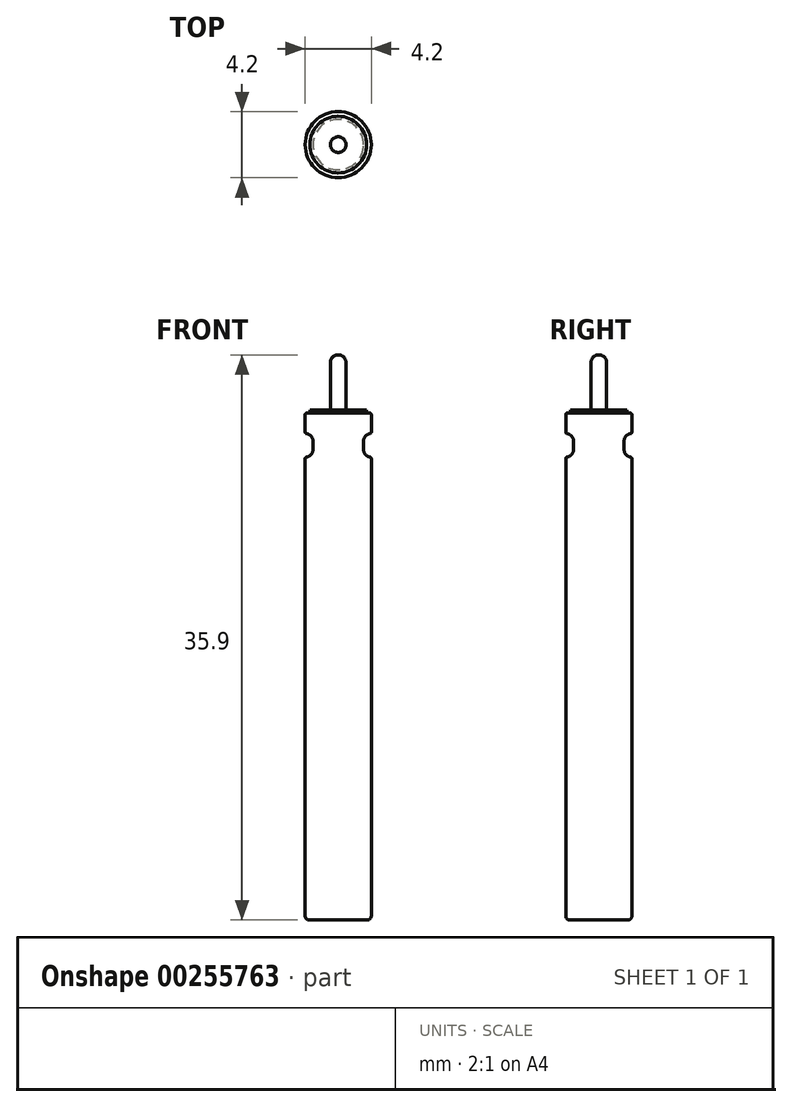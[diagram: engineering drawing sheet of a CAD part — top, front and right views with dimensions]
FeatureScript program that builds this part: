
annotation { "Feature Type Name" : "Feature", "Feature Type Description" : "" }
export const myFeature = defineFeature(function(context is Context, id is Id, definition is map)
    precondition{}
    {
        {
            var Q0;
            Q0=qCreatedBy(makeId("Front.planeOp"),FACE);
            var sketch = newSketch(context, id + "F0", { "sketchPlane" : qUnion([Q0])});
            skLineSegment(sketch, "E0", {"start": v(0, 3.7) * mm, "end": v(0, -32.2) * mm});
            skLineSegment(sketch, "E1", {"start": v(0, -32.2) * mm, "end": v(1.85, -32.2) * mm});
            skLineSegment(sketch, "E2", {"start": v(2.1, -31.95) * mm, "end": v(2.1, -2.8) * mm});
            skLineSegment(sketch, "E3", {"start": v(2.1, -2.8) * mm, "end": v(2.1, -2.8) * mm});
            skLineSegment(sketch, "E4", {"start": v(1.6, -2.3) * mm, "end": v(1.6, -1.8) * mm});
            skLineSegment(sketch, "E5", {"start": v(2.1, -1.3) * mm, "end": v(2.1, -1.3) * mm});
            skLineSegment(sketch, "E6", {"start": v(2.1, -1.3) * mm, "end": v(2.1, 0) * mm});
            skLineSegment(sketch, "E7", {"start": v(2.1, 0) * mm, "end": v(1.8, 0) * mm});
            skLineSegment(sketch, "E8", {"start": v(1.8, 0) * mm, "end": v(1.8, 0.2) * mm});
            skLineSegment(sketch, "E9", {"start": v(1.8, 0.2) * mm, "end": v(0.5, 0.2) * mm});
            skLineSegment(sketch, "E10", {"start": v(0.5, 0.2) * mm, "end": v(0.5, 3.7) * mm});
            skLineSegment(sketch, "E11", {"start": v(0.5, 3.7) * mm, "end": v(0, 3.7) * mm});
            skPoint(sketch, "E12.orphan", {"position": v(0, 12.96) * mm});
            skPoint(sketch, "E13.visualSharp", {"position": v(1.6, -2.8) * mm});
            skArc(sketch, "E13.filletArc", {"start": v(1.6, -2.3) * mm, "mid": v(1.75, -2.65) * mm, "end": v(2.1, -2.8) * mm});
            skPoint(sketch, "E14.visualSharp", {"position": v(2.1, -32.2) * mm});
            skArc(sketch, "E14.filletArc", {"start": v(1.85, -32.2) * mm, "mid": v(2.03, -32.13) * mm, "end": v(2.1, -31.95) * mm});
            skPoint(sketch, "E15.visualSharp", {"position": v(1.6, -1.3) * mm});
            skArc(sketch, "E15.filletArc", {"start": v(2.1, -1.3) * mm, "mid": v(1.75, -1.45) * mm, "end": v(1.6, -1.8) * mm});
            skSolve(sketch);
        }
        {
            var Q0;
            Q0=makeQuery(id+"F0.imprint","IMPRINT",FACE,{"disambiguationData":[TD([[makeQuery(id+"F0.imprint","IMPRINT",EDGE,{"derivedFrom":sQuery(id+"F0.wireOp",EDGE,"E0")}),1.0]])]});
            var Q1;
            Q1=sQuery(id+"F0.wireOp",EDGE,"E0");
            revolve(context, id + "F1", {"entities" : qUnion([Q0]), "axis" : qUnion([Q1]), "revolveType" : RevolveType.FULL});
        }
        {
            var Q0;
            Q0=makeQuery(id+"F1.opRevolve","SWEPT_EDGE",EDGE,{"disambiguationData":[OSD([sQuery(id+"F0.wireOp",EDGE,"E2"),sQuery(id+"F0.wireOp",EDGE,"E13.filletArc")])]});
            var Q1;
            Q1=makeQuery(id+"F1.opRevolve","SWEPT_EDGE",EDGE,{"disambiguationData":[OSD([sQuery(id+"F0.wireOp",EDGE,"E6"),sQuery(id+"F0.wireOp",EDGE,"E15.filletArc")])]});
            var Q2;
            Q2=makeQuery(id+"F1.opRevolve","SWEPT_EDGE",EDGE,{"disambiguationData":[OSD([sQuery(id+"F0.wireOp",EDGE,"E6"),sQuery(id+"F0.wireOp",EDGE,"E7")])]});
            fillet(context, id + "F2", {"entities" : qUnion([Q0, Q1, Q2]), "radius" : .1 * mm, "tangentPropagation" : true, "allowEdgeOverflow" : false});
        }
        {
            var Q0;
            Q0=makeQuery(id+"F1.opRevolve","SWEPT_EDGE",EDGE,{"disambiguationData":[OSD([sQuery(id+"F0.wireOp",EDGE,"E10"),sQuery(id+"F0.wireOp",EDGE,"E11")])]});
            fillet(context, id + "F3", {"entities" : qUnion([Q0]), "radius" : .5 * mm, "tangentPropagation" : true, "allowEdgeOverflow" : false});
        }
    });
